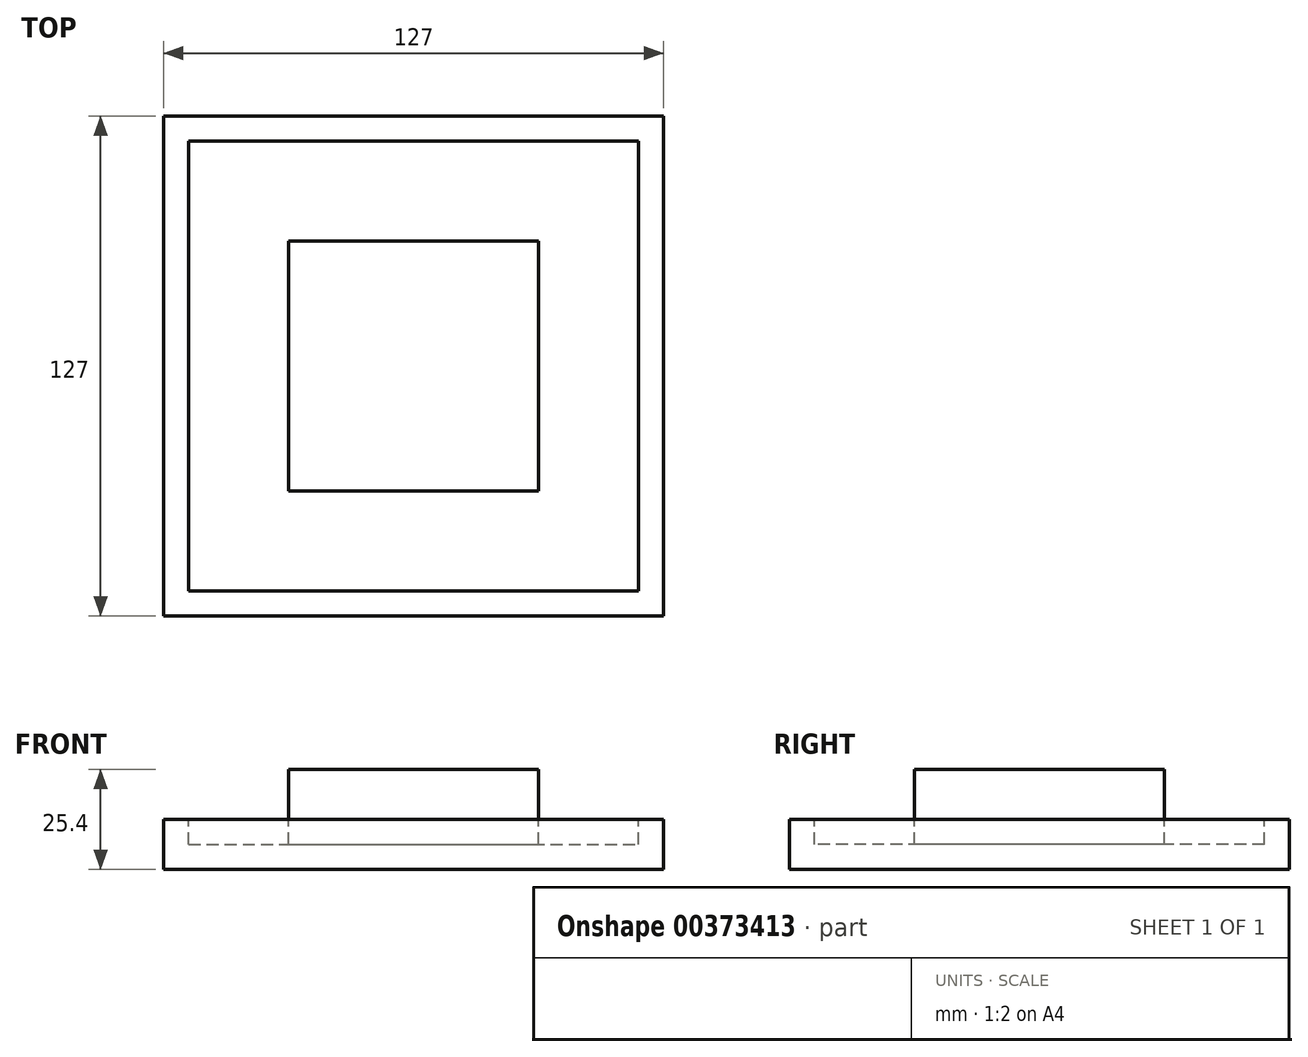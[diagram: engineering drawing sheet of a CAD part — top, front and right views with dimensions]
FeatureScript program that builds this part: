
annotation { "Feature Type Name" : "Feature", "Feature Type Description" : "" }
export const myFeature = defineFeature(function(context is Context, id is Id, definition is map)
    precondition{}
    {
        {
            var Q0;
            Q0=qCreatedBy(makeId("Top.planeOp"),FACE);
            var sketch = newSketch(context, id + "F0", { "sketchPlane" : qUnion([Q0])});
            skLineSegment(sketch, "E0.bottom", {"start": v(-63.5, 63.5) * mm, "end": v(63.5, 63.5) * mm});
            skLineSegment(sketch, "E0.top", {"start": v(-63.5, -63.5) * mm, "end": v(63.5, -63.5) * mm});
            skLineSegment(sketch, "E0.left", {"start": v(-63.5, 63.5) * mm, "end": v(-63.5, -63.5) * mm});
            skLineSegment(sketch, "E0.right", {"start": v(63.5, 63.5) * mm, "end": v(63.5, -63.5) * mm});
            skLineSegment(sketch, "E1", {"start": v(-63.5, 63.5) * mm, "end": v(63.5, -63.5) * mm, "construction": true});
            skLineSegment(sketch, "E2", {"start": v(63.5, 63.5) * mm, "end": v(-63.5, -63.5) * mm, "construction": true});
            skSolve(sketch);
        }
        {
            var Q0;
            Q0=makeQuery(id+"F0.imprint","IMPRINT",FACE,{"disambiguationData":[TD([[makeQuery(id+"F0.imprint","IMPRINT",EDGE,{"derivedFrom":sQuery(id+"F0.wireOp",EDGE,"E0.bottom")}),-1.0]])]});
            extrude(context, id + "F1", {"entities" : qUnion([Q0]), "depth" : 12.7 * mm});
        }
        {
            var Q0;
            Q0=makeQuery(id+"F1.opExtrude","CAP_FACE",FACE,{"disambiguationData":[OSD([sQuery(id+"F0.wireOp",EDGE,"E0.bottom"),sQuery(id+"F0.wireOp",EDGE,"E0.top"),sQuery(id+"F0.wireOp",EDGE,"E0.left"),sQuery(id+"F0.wireOp",EDGE,"E0.right")])],"isStart":false});
            var sketch = newSketch(context, id + "F2", { "sketchPlane" : qUnion([Q0])});
            skLineSegment(sketch, "E3.bottom", {"start": v(-57.15, 57.15) * mm, "end": v(57.15, 57.15) * mm});
            skLineSegment(sketch, "E3.top", {"start": v(-57.15, -57.15) * mm, "end": v(57.15, -57.15) * mm});
            skLineSegment(sketch, "E3.left", {"start": v(-57.15, 57.15) * mm, "end": v(-57.15, -57.15) * mm});
            skLineSegment(sketch, "E3.right", {"start": v(57.15, 57.15) * mm, "end": v(57.15, -57.15) * mm});
            skLineSegment(sketch, "E4.bottom", {"start": v(-31.75, 31.75) * mm, "end": v(31.75, 31.75) * mm});
            skLineSegment(sketch, "E4.top", {"start": v(-31.75, -31.75) * mm, "end": v(31.75, -31.75) * mm});
            skLineSegment(sketch, "E4.left", {"start": v(-31.75, 31.75) * mm, "end": v(-31.75, -31.75) * mm});
            skLineSegment(sketch, "E4.right", {"start": v(31.75, 31.75) * mm, "end": v(31.75, -31.75) * mm});
            skLineSegment(sketch, "E5", {"start": v(-57.15, 57.15) * mm, "end": v(57.15, -57.15) * mm, "construction": true});
            skLineSegment(sketch, "E6", {"start": v(-57.15, -57.15) * mm, "end": v(57.15, 57.15) * mm, "construction": true});
            skSolve(sketch);
        }
        {
            var Q0;
            Q0=makeQuery(id+"F2.imprint","IMPRINT",FACE,{"disambiguationData":[TD([[makeQuery(id+"F2.imprint","IMPRINT",EDGE,{"derivedFrom":sQuery(id+"F2.wireOp",EDGE,"E3.bottom")}),-1.0]])]});
            extrude(context, id + "F3", {"entities" : qUnion([Q0]), "operationType" : NewBodyOperationType.REMOVE, "oppositeDirection" : true, "depth" : 6.35 * mm});
        }
        {
            var Q0;
            Q0=makeQuery(id+"F3.boolean.opBoolean","SPLIT",FACE,{"disambiguationData":[TD([makeQuery(id+"F3.opExtrude","SWEPT_FACE",FACE,{"disambiguationData":[OSD([sQuery(id+"F2.wireOp",EDGE,"E4.bottom")])]})])],"derivedFrom":makeQuery(id+"F1.opExtrude","CAP_FACE",FACE,{"disambiguationData":[OSD([sQuery(id+"F0.wireOp",EDGE,"E0.bottom"),sQuery(id+"F0.wireOp",EDGE,"E0.top"),sQuery(id+"F0.wireOp",EDGE,"E0.left"),sQuery(id+"F0.wireOp",EDGE,"E0.right")])],"isStart":false})});
            extrude(context, id + "F4", {"entities" : qUnion([Q0]), "operationType" : NewBodyOperationType.ADD, "depth" : 12.7 * mm});
        }
    });
